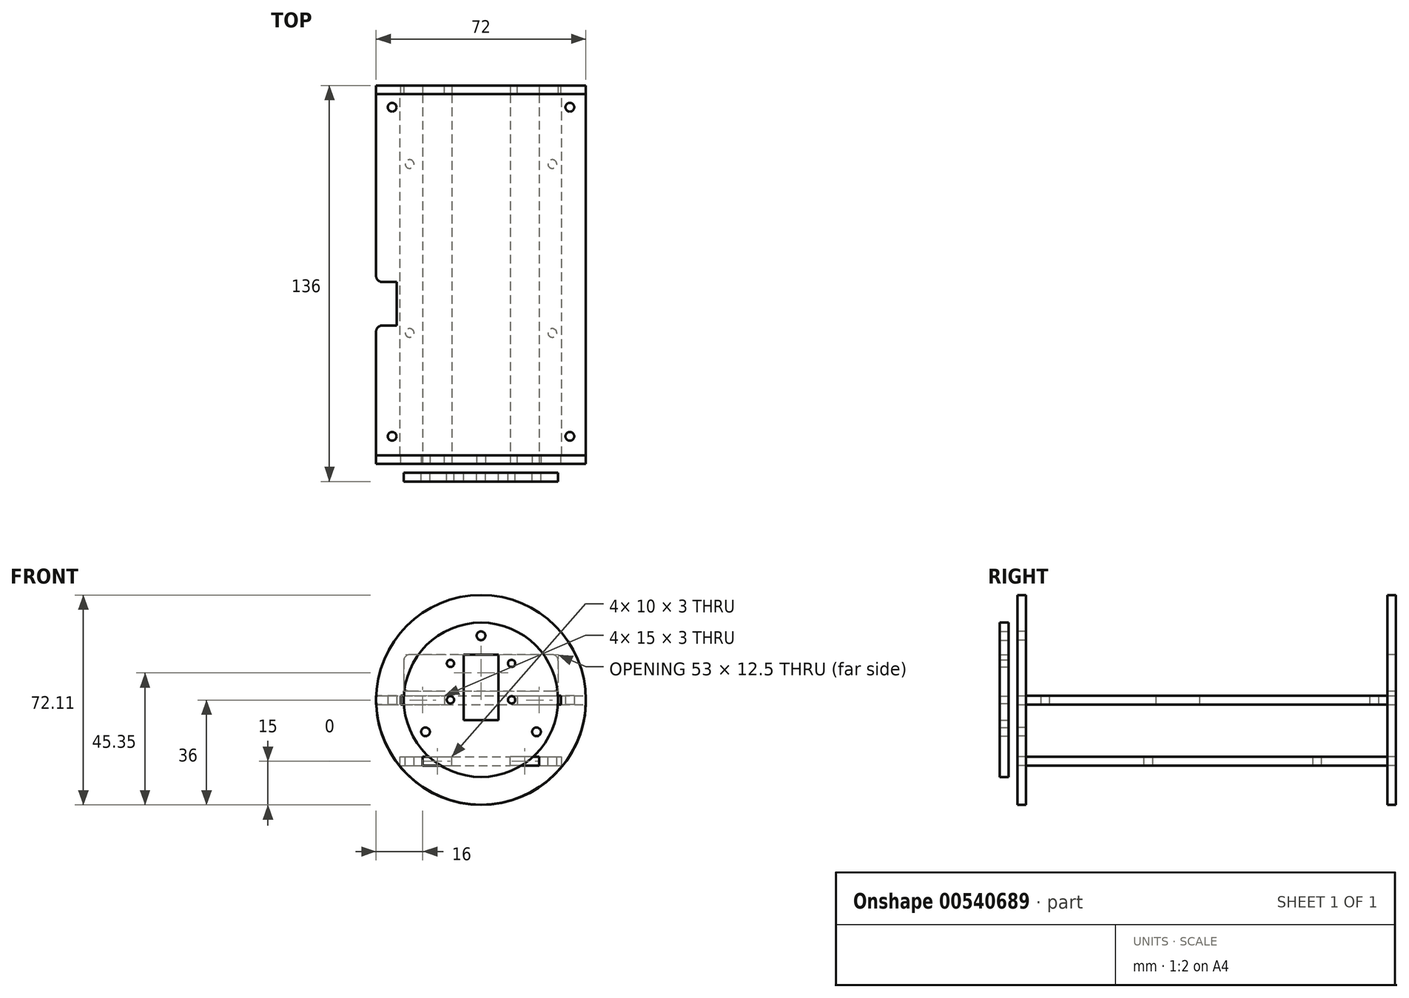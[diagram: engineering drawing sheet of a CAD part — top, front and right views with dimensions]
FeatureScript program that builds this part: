
annotation { "Feature Type Name" : "Feature", "Feature Type Description" : "" }
export const myFeature = defineFeature(function(context is Context, id is Id, definition is map)
    precondition{}
    {
        {
            var Q0;
            Q0=qCreatedBy(makeId("Top.planeOp"),FACE);
            var sketch = newSketch(context, id + "F0", { "sketchPlane" : qUnion([Q0])});
            skLineSegment(sketch, "E0.bottom", {"start": v(-34, 61) * mm, "end": v(34, 61) * mm, "construction": true});
            skLineSegment(sketch, "E0.top", {"start": v(-34, -59) * mm, "end": v(34, -59) * mm, "construction": true});
            skLineSegment(sketch, "E0.left", {"start": v(-34, 61) * mm, "end": v(-34, -59) * mm, "construction": true});
            skLineSegment(sketch, "E0.right", {"start": v(34, 61) * mm, "end": v(34, -59) * mm, "construction": true});
            skPoint(sketch, "E0.middle", {"position": v(0, 0) * mm});
            skCircle(sketch, "E1", {"center": v(-30.5, 57.5) * mm, "radius": 1.5 * mm});
            skCircle(sketch, "E2", {"center": v(30.5, 57.5) * mm, "radius": 1.5 * mm});
            skCircle(sketch, "E3", {"center": v(-30.5, -55.5) * mm, "radius": 1.5 * mm});
            skCircle(sketch, "E4", {"center": v(30.5, -55.5) * mm, "radius": 1.5 * mm});
            skLineSegment(sketch, "E5.bottom", {"start": v(-36, 62) * mm, "end": v(36, 62) * mm});
            skLineSegment(sketch, "E5.top", {"start": v(-36, -62) * mm, "end": v(36, -62) * mm});
            skLineSegment(sketch, "E5.left", {"start": v(-36, 62) * mm, "end": v(-36, -62) * mm});
            skLineSegment(sketch, "E5.right", {"start": v(36, 62) * mm, "end": v(36, -62) * mm});
            skLineSegment(sketch, "E6.bottom", {"start": v(-24, -3.98) * mm, "end": v(-34, -3.98) * mm, "construction": true});
            skLineSegment(sketch, "E6.top", {"start": v(-24, -15.98) * mm, "end": v(-34, -15.98) * mm, "construction": true});
            skLineSegment(sketch, "E6.left", {"start": v(-24, -3.98) * mm, "end": v(-24, -15.98) * mm, "construction": true});
            skLineSegment(sketch, "E6.right", {"start": v(-34, -3.98) * mm, "end": v(-34, -15.98) * mm, "construction": true});
            skPoint(sketch, "E6.middle", {"position": v(-29, -9.98) * mm});
            skLineSegment(sketch, "E7", {"start": v(-36, -2.48) * mm, "end": v(-29, -2.48) * mm});
            skPoint(sketch, "E7.endSnap0", {"position": v(-29, -3.98) * mm});
            skLineSegment(sketch, "E8", {"start": v(-29, -2.48) * mm, "end": v(-29, -17.48) * mm});
            skLineSegment(sketch, "E9", {"start": v(-29, -17.48) * mm, "end": v(-36, -17.48) * mm});
            skLineSegment(sketch, "E10.bottom", {"start": v(27.5, -62) * mm, "end": v(12.5, -62) * mm});
            skLineSegment(sketch, "E10.top", {"start": v(27.5, -65) * mm, "end": v(12.5, -65) * mm});
            skLineSegment(sketch, "E10.left", {"start": v(27.5, -62) * mm, "end": v(27.5, -65) * mm});
            skLineSegment(sketch, "E10.right", {"start": v(12.5, -62) * mm, "end": v(12.5, -65) * mm});
            skPoint(sketch, "E10.middle", {"position": v(20, -63.5) * mm});
            skLineSegment(sketch, "E11", {"start": v(22.63, 0) * mm, "end": v(0, 0) * mm, "construction": true});
            skLineSegment(sketch, "E12", {"start": v(0, 0) * mm, "end": v(0, -27.49) * mm, "construction": true});
            skLineSegment(sketch, "E13.MirrorCS", {"start": v(27.5, 62) * mm, "end": v(27.5, 65) * mm});
            skLineSegment(sketch, "E14.MirrorCS", {"start": v(27.5, 65) * mm, "end": v(12.5, 65) * mm});
            skLineSegment(sketch, "E15.MirrorCS", {"start": v(12.5, 62) * mm, "end": v(12.5, 65) * mm});
            skLineSegment(sketch, "E16.MirrorCS", {"start": v(-27.5, 62) * mm, "end": v(-27.5, 65) * mm});
            skLineSegment(sketch, "E17.MirrorCS", {"start": v(-27.5, 65) * mm, "end": v(-12.5, 65) * mm});
            skLineSegment(sketch, "E18.MirrorCS", {"start": v(-12.5, 62) * mm, "end": v(-12.5, 65) * mm});
            skLineSegment(sketch, "E19.MirrorCS", {"start": v(-27.5, -62) * mm, "end": v(-27.5, -65) * mm});
            skLineSegment(sketch, "E20.MirrorCS", {"start": v(-27.5, -65) * mm, "end": v(-12.5, -65) * mm});
            skLineSegment(sketch, "E21.MirrorCS", {"start": v(-12.5, -62) * mm, "end": v(-12.5, -65) * mm});
            skSolve(sketch);
        }
        {
            var Q0;
            Q0=makeQuery(id+"F0.imprint","IMPRINT",FACE,{"disambiguationData":[TD([[makeQuery(id+"F0.imprint","IMPRINT",EDGE,{"derivedFrom":sQuery(id+"F0.wireOp",EDGE,"E1")}),-1.0]])]});
            var Q1;
            {var subQ0=sQuery(id+"F0.wireOp",EDGE,"E13.MirrorCS");Q1=makeQuery(id+"F0.imprint","IMPRINT",FACE,{"disambiguationData":[TD([[makeQuery(id+"F0.imprint","IMPRINT",EDGE,{"derivedFrom":subQ0}),1.0]])]});}
            var Q2;
            {var subQ0=sQuery(id+"F0.wireOp",EDGE,"E16.MirrorCS");Q2=makeQuery(id+"F0.imprint","IMPRINT",FACE,{"disambiguationData":[TD([[makeQuery(id+"F0.imprint","IMPRINT",EDGE,{"derivedFrom":subQ0}),-1.0]])]});}
            var Q3;
            Q3=makeQuery(id+"F0.imprint","IMPRINT",FACE,{"disambiguationData":[TD([[makeQuery(id+"F0.imprint","IMPRINT",EDGE,{"derivedFrom":sQuery(id+"F0.wireOp",EDGE,"E10.bottom")}),1.0]])]});
            var Q4;
            {var subQ0=sQuery(id+"F0.wireOp",EDGE,"E19.MirrorCS");Q4=makeQuery(id+"F0.imprint","IMPRINT",FACE,{"disambiguationData":[TD([[makeQuery(id+"F0.imprint","IMPRINT",EDGE,{"derivedFrom":subQ0}),1.0]])]});}
            extrude(context, id + "F1", {"entities" : qUnion([Q0, Q1, Q2, Q3, Q4]), "depth" : 3 * mm});
        }
        {
            var Q0;
            Q0=makeQuery(id+"F1.opExtrude","SWEPT_EDGE",EDGE,{"disambiguationData":[OSD([sQuery(id+"F0.wireOp",EDGE,"E5.left"),sQuery(id+"F0.wireOp",EDGE,"E7")])]});
            var Q1;
            Q1=makeQuery(id+"F1.opExtrude","SWEPT_EDGE",EDGE,{"disambiguationData":[OSD([sQuery(id+"F0.wireOp",EDGE,"E5.left"),sQuery(id+"F0.wireOp",EDGE,"E9")])]});
            fillet(context, id + "F2", {"entities" : qUnion([Q0, Q1]), "radius" : 2 * mm, "tangentPropagation" : true, "allowEdgeOverflow" : false});
        }
        {
            var Q0;
            {var subQ0=sQuery(id+"F0.wireOp",EDGE,"E5.top");Q0=makeQuery(id+"F1.opExtrude","SWEPT_FACE",FACE,{"disambiguationData":[OSD([subQ0]),TDD([makeQuery(id+"F0.imprint","IMPRINT",EDGE,{"disambiguationData":[TD([[makeQuery(id+"F0.imprint","INTERSECT",VERTEX,{"derivedFrom":[subQ0,sQuery(id+"F0.wireOp",EDGE,"E21.MirrorCS")]}),-1.0]])],"derivedFrom":subQ0})])]});}
            var sketch = newSketch(context, id + "F3", { "sketchPlane" : qUnion([Q0])});
            skCircle(sketch, "E22", {"center": v(0, 1.61) * mm, "radius": 36 * mm});
            skLineSegment(sketch, "E23", {"start": v(0, 0) * mm, "end": v(0, 3) * mm, "construction": true});
            skLineSegment(sketch, "E24.0", {"start": v(-27.5, 3) * mm, "end": v(-12.5, 3) * mm});
            skLineSegment(sketch, "E24.1", {"start": v(-27.5, 3) * mm, "end": v(-27.5, 0) * mm});
            skLineSegment(sketch, "E24.2", {"start": v(-27.5, 0) * mm, "end": v(-12.5, 0) * mm});
            skLineSegment(sketch, "E24.3", {"start": v(-12.5, 3) * mm, "end": v(-12.5, 0) * mm});
            skLineSegment(sketch, "E24.4", {"start": v(27.5, 3) * mm, "end": v(12.5, 3) * mm});
            skLineSegment(sketch, "E24.5", {"start": v(12.5, 3) * mm, "end": v(12.5, 0) * mm});
            skLineSegment(sketch, "E24.6", {"start": v(27.5, 0) * mm, "end": v(12.5, 0) * mm});
            skLineSegment(sketch, "E24.7", {"start": v(27.5, 3) * mm, "end": v(27.5, 0) * mm});
            skSolve(sketch);
        }
        {
            var Q0;
            Q0=qSketchRegion(id+"F3",true);
            extrude(context, id + "F4", {"entities" : qUnion([Q0]), "depth" : 3 * mm});
        }
        {
            var Q0;
            {var subQ0=sQuery(id+"F0.wireOp",EDGE,"E5.bottom");Q0=makeQuery(id+"F1.opExtrude","SWEPT_FACE",FACE,{"disambiguationData":[OSD([subQ0]),TDD([makeQuery(id+"F0.imprint","IMPRINT",EDGE,{"disambiguationData":[TD([[makeQuery(id+"F0.imprint","INTERSECT",VERTEX,{"derivedFrom":[subQ0,sQuery(id+"F0.wireOp",EDGE,"E15.MirrorCS")]}),1.0]])],"derivedFrom":subQ0})])]});}
            var sketch = newSketch(context, id + "F5", { "sketchPlane" : qUnion([Q0])});
            skLineSegment(sketch, "E25", {"start": v(0, 0) * mm, "end": v(0, 3) * mm, "construction": true});
            skPoint(sketch, "E26", {"position": v(0, 1.5) * mm});
            skCircle(sketch, "E27", {"center": v(0, 1.5) * mm, "radius": 36 * mm});
            skLineSegment(sketch, "E28.0", {"start": v(-27.5, 3) * mm, "end": v(-12.5, 3) * mm});
            skLineSegment(sketch, "E28.1", {"start": v(-27.5, 3) * mm, "end": v(-27.5, 0) * mm});
            skLineSegment(sketch, "E28.2", {"start": v(-27.5, 0) * mm, "end": v(-12.5, 0) * mm});
            skLineSegment(sketch, "E28.3", {"start": v(-12.5, 3) * mm, "end": v(-12.5, 0) * mm});
            skLineSegment(sketch, "E28.4", {"start": v(27.5, 3) * mm, "end": v(12.5, 3) * mm});
            skLineSegment(sketch, "E28.5", {"start": v(12.5, 3) * mm, "end": v(12.5, 0) * mm});
            skLineSegment(sketch, "E28.6", {"start": v(27.5, 0) * mm, "end": v(12.5, 0) * mm});
            skLineSegment(sketch, "E28.7", {"start": v(27.5, 3) * mm, "end": v(27.5, 0) * mm});
            skLineSegment(sketch, "E29.bottom", {"start": v(-24.5, 17.1) * mm, "end": v(24.5, 17.1) * mm});
            skLineSegment(sketch, "E29.top", {"start": v(-24.5, 4.6) * mm, "end": v(24.5, 4.6) * mm});
            skLineSegment(sketch, "E29.left", {"start": v(-26.5, 15.1) * mm, "end": v(-26.5, 6.6) * mm});
            skLineSegment(sketch, "E29.right", {"start": v(26.5, 15.1) * mm, "end": v(26.5, 6.6) * mm});
            skPoint(sketch, "E29.middle", {"position": v(0, 10.85) * mm});
            skPoint(sketch, "E30.visualSharp", {"position": v(-26.5, 17.1) * mm});
            skArc(sketch, "E30.filletArc", {"start": v(-24.5, 17.1) * mm, "mid": v(-25.91, 16.51) * mm, "end": v(-26.5, 15.1) * mm});
            skPoint(sketch, "E31.visualSharp", {"position": v(-26.5, 4.6) * mm});
            skArc(sketch, "E31.filletArc", {"start": v(-26.5, 6.6) * mm, "mid": v(-25.91, 5.19) * mm, "end": v(-24.5, 4.6) * mm});
            skPoint(sketch, "E32.visualSharp", {"position": v(26.5, 4.6) * mm});
            skArc(sketch, "E32.filletArc", {"start": v(24.5, 4.6) * mm, "mid": v(25.91, 5.19) * mm, "end": v(26.5, 6.6) * mm});
            skPoint(sketch, "E33.visualSharp", {"position": v(26.5, 17.1) * mm});
            skArc(sketch, "E33.filletArc", {"start": v(26.5, 15.1) * mm, "mid": v(25.91, 16.51) * mm, "end": v(24.5, 17.1) * mm});
            skSolve(sketch);
        }
        {
            var Q0;
            Q0=qSketchRegion(id+"F5",true);
            extrude(context, id + "F6", {"entities" : qUnion([Q0]), "depth" : 3 * mm});
        }
        {
            var Q0;
            Q0=makeQuery(id+"F1.opExtrude","CAP_FACE",FACE,{"disambiguationData":[OSD([sQuery(id+"F0.wireOp",EDGE,"E1"),sQuery(id+"F0.wireOp",EDGE,"E2"),sQuery(id+"F0.wireOp",EDGE,"E3"),sQuery(id+"F0.wireOp",EDGE,"E4"),sQuery(id+"F0.wireOp",EDGE,"E5.bottom"),sQuery(id+"F0.wireOp",EDGE,"E5.top"),sQuery(id+"F0.wireOp",EDGE,"E5.left"),sQuery(id+"F0.wireOp",EDGE,"E5.right"),sQuery(id+"F0.wireOp",EDGE,"E7"),sQuery(id+"F0.wireOp",EDGE,"E8"),sQuery(id+"F0.wireOp",EDGE,"E9"),sQuery(id+"F0.wireOp",EDGE,"E10.top"),sQuery(id+"F0.wireOp",EDGE,"E10.left"),sQuery(id+"F0.wireOp",EDGE,"E10.right"),sQuery(id+"F0.wireOp",EDGE,"E13.MirrorCS"),sQuery(id+"F0.wireOp",EDGE,"E14.MirrorCS"),sQuery(id+"F0.wireOp",EDGE,"E15.MirrorCS"),sQuery(id+"F0.wireOp",EDGE,"E16.MirrorCS"),sQuery(id+"F0.wireOp",EDGE,"E17.MirrorCS"),sQuery(id+"F0.wireOp",EDGE,"E18.MirrorCS"),sQuery(id+"F0.wireOp",EDGE,"E19.MirrorCS"),sQuery(id+"F0.wireOp",EDGE,"E20.MirrorCS"),sQuery(id+"F0.wireOp",EDGE,"E21.MirrorCS")])],"isStart":true});
            cPlane(context, id + "F7", {"entities" : qUnion([Q0]), "cplaneType" : CPlaneType.OFFSET, "offset" : 18 * mm, "width" : 150 * mm, "height" : 150 * mm});
        }
        {
            var Q0;
            Q0=qCreatedBy(id+"F7.planeOp",FACE);
            var sketch = newSketch(context, id + "F8", { "sketchPlane" : qUnion([Q0])});
            skLineSegment(sketch, "E34.bottom", {"start": v(-27.75, 62) * mm, "end": v(27.75, 62) * mm});
            skLineSegment(sketch, "E34.top", {"start": v(-27.75, -62) * mm, "end": v(27.75, -62) * mm});
            skLineSegment(sketch, "E34.left", {"start": v(-27.75, 62) * mm, "end": v(-27.75, -62) * mm});
            skLineSegment(sketch, "E34.right", {"start": v(27.75, 62) * mm, "end": v(27.75, -62) * mm});
            skPoint(sketch, "E34.middle", {"position": v(0, 0) * mm});
            skLineSegment(sketch, "E35.bottom", {"start": v(-20, 62) * mm, "end": v(-10, 62) * mm});
            skLineSegment(sketch, "E35.top", {"start": v(-20, 65) * mm, "end": v(-10, 65) * mm});
            skLineSegment(sketch, "E35.left", {"start": v(-20, 62) * mm, "end": v(-20, 65) * mm});
            skLineSegment(sketch, "E35.right", {"start": v(-10, 62) * mm, "end": v(-10, 65) * mm});
            skPoint(sketch, "E35.middle", {"position": v(-15, 63.5) * mm});
            skLineSegment(sketch, "E36", {"start": v(0, 27.21) * mm, "end": v(0, 0) * mm, "construction": true});
            skLineSegment(sketch, "E37", {"start": v(0, 0) * mm, "end": v(20.44, 0) * mm, "construction": true});
            skLineSegment(sketch, "E38.MirrorCS", {"start": v(10, 62) * mm, "end": v(10, 65) * mm});
            skLineSegment(sketch, "E39.MirrorCS", {"start": v(20, 65) * mm, "end": v(10, 65) * mm});
            skLineSegment(sketch, "E40.MirrorCS", {"start": v(20, 62) * mm, "end": v(20, 65) * mm});
            skLineSegment(sketch, "E41.MirrorCS", {"start": v(20, -62) * mm, "end": v(20, -65) * mm});
            skLineSegment(sketch, "E42.MirrorCS", {"start": v(20, -65) * mm, "end": v(10, -65) * mm});
            skLineSegment(sketch, "E43.MirrorCS", {"start": v(10, -62) * mm, "end": v(10, -65) * mm});
            skLineSegment(sketch, "E44.MirrorCS", {"start": v(-10, -62) * mm, "end": v(-10, -65) * mm});
            skLineSegment(sketch, "E45.MirrorCS", {"start": v(-20, -65) * mm, "end": v(-10, -65) * mm});
            skLineSegment(sketch, "E46.MirrorCS", {"start": v(-20, -62) * mm, "end": v(-20, -65) * mm});
            skCircle(sketch, "E47", {"center": v(24.5, 20) * mm, "radius": 1.5 * mm});
            skCircle(sketch, "E48", {"center": v(24.5, -38) * mm, "radius": 1.5 * mm});
            skCircle(sketch, "E49", {"center": v(-24.5, -38) * mm, "radius": 1.5 * mm});
            skCircle(sketch, "E50", {"center": v(-24.5, 20) * mm, "radius": 1.5 * mm});
            skLineSegment(sketch, "E51", {"start": v(24.5, 20) * mm, "end": v(-24.5, 20) * mm, "construction": true});
            skPoint(sketch, "E52", {"position": v(0, 20) * mm});
            skSolve(sketch);
        }
        {
            var Q0;
            Q0=qSketchRegion(id+"F8",true);
            extrude(context, id + "F9", {"entities" : qUnion([Q0]), "depth" : 3 * mm});
        }
        {
            var Q0;
            Q0=makeQuery(id+"F4.opExtrude","CAP_FACE",FACE,{"disambiguationData":[OSD([sQuery(id+"F3.wireOp",EDGE,"E22"),sQuery(id+"F3.wireOp",EDGE,"E24.0"),sQuery(id+"F3.wireOp",EDGE,"E24.1"),sQuery(id+"F3.wireOp",EDGE,"E24.2"),sQuery(id+"F3.wireOp",EDGE,"E24.3"),sQuery(id+"F3.wireOp",EDGE,"E24.4"),sQuery(id+"F3.wireOp",EDGE,"E24.5"),sQuery(id+"F3.wireOp",EDGE,"E24.6"),sQuery(id+"F3.wireOp",EDGE,"E24.7")])],"isStart":false});
            var sketch = newSketch(context, id + "F10", { "sketchPlane" : qUnion([Q0])});
            skLineSegment(sketch, "E53.0", {"start": v(-20, -18) * mm, "end": v(-10, -18) * mm});
            skLineSegment(sketch, "E53.1", {"start": v(-20, -21) * mm, "end": v(-20, -18) * mm});
            skLineSegment(sketch, "E53.2", {"start": v(-20, -21) * mm, "end": v(-10, -21) * mm});
            skLineSegment(sketch, "E53.3", {"start": v(-10, -21) * mm, "end": v(-10, -18) * mm});
            skLineSegment(sketch, "E53.4", {"start": v(20, -18) * mm, "end": v(10, -18) * mm});
            skLineSegment(sketch, "E53.5", {"start": v(10, -21) * mm, "end": v(10, -18) * mm});
            skLineSegment(sketch, "E53.6", {"start": v(20, -21) * mm, "end": v(10, -21) * mm});
            skLineSegment(sketch, "E53.7", {"start": v(20, -21) * mm, "end": v(20, -18) * mm});
            skSolve(sketch);
        }
        {
            var Q0;
            Q0=qSketchRegion(id+"F10",true);
            var Q1;
            Q1=makeQuery(id+"F6.opExtrude","CAP_FACE",FACE,{"disambiguationData":[OSD([sQuery(id+"F5.wireOp",EDGE,"E27"),sQuery(id+"F5.wireOp",EDGE,"E28.0"),sQuery(id+"F5.wireOp",EDGE,"E28.1"),sQuery(id+"F5.wireOp",EDGE,"E28.2"),sQuery(id+"F5.wireOp",EDGE,"E28.3"),sQuery(id+"F5.wireOp",EDGE,"E28.4"),sQuery(id+"F5.wireOp",EDGE,"E28.5"),sQuery(id+"F5.wireOp",EDGE,"E28.6"),sQuery(id+"F5.wireOp",EDGE,"E28.7"),sQuery(id+"F5.wireOp",EDGE,"E29.bottom"),sQuery(id+"F5.wireOp",EDGE,"E29.top"),sQuery(id+"F5.wireOp",EDGE,"E29.left"),sQuery(id+"F5.wireOp",EDGE,"E29.right"),sQuery(id+"F5.wireOp",EDGE,"E30.filletArc"),sQuery(id+"F5.wireOp",EDGE,"E31.filletArc"),sQuery(id+"F5.wireOp",EDGE,"E32.filletArc"),sQuery(id+"F5.wireOp",EDGE,"E33.filletArc")])],"isStart":false});
            extrude(context, id + "F11", {"entities" : qUnion([Q0]), "operationType" : NewBodyOperationType.REMOVE, "endBound" : BoundingType.UP_TO_SURFACE, "oppositeDirection" : true, "endBoundEntityFace" : qUnion([Q1]), "depth" : 25 * mm});
        }
        {
            var Q0;
            Q0=makeQuery(id+"F4.opExtrude","CAP_FACE",FACE,{"disambiguationData":[OSD([sQuery(id+"F3.wireOp",EDGE,"E22"),sQuery(id+"F3.wireOp",EDGE,"E24.0"),sQuery(id+"F3.wireOp",EDGE,"E24.1"),sQuery(id+"F3.wireOp",EDGE,"E24.2"),sQuery(id+"F3.wireOp",EDGE,"E24.3"),sQuery(id+"F3.wireOp",EDGE,"E24.4"),sQuery(id+"F3.wireOp",EDGE,"E24.5"),sQuery(id+"F3.wireOp",EDGE,"E24.6"),sQuery(id+"F3.wireOp",EDGE,"E24.7")])],"isStart":false});
            cPlane(context, id + "F12", {"entities" : qUnion([Q0]), "cplaneType" : CPlaneType.OFFSET, "offset" : 3 * mm, "width" : 150 * mm, "height" : 150 * mm});
        }
        {
            var Q0;
            Q0=qCreatedBy(id+"F12.planeOp",FACE);
            var sketch = newSketch(context, id + "F13", { "sketchPlane" : qUnion([Q0])});
            skCircle(sketch, "E54.0", {"center": v(0, 1.61) * mm, "radius": 36 * mm, "construction": true});
            skLineSegment(sketch, "E55.bottom", {"start": v(-4, 5.61) * mm, "end": v(4, 5.61) * mm, "construction": true});
            skLineSegment(sketch, "E55.top", {"start": v(-4, -2.39) * mm, "end": v(4, -2.39) * mm, "construction": true});
            skLineSegment(sketch, "E55.left", {"start": v(-4, 5.61) * mm, "end": v(-4, -2.39) * mm, "construction": true});
            skLineSegment(sketch, "E55.right", {"start": v(4, 5.61) * mm, "end": v(4, -2.39) * mm, "construction": true});
            skCircle(sketch, "E56", {"center": v(-10.5, 1.61) * mm, "radius": 1.25 * mm});
            skCircle(sketch, "E57", {"center": v(10.5, 1.61) * mm, "radius": 1.25 * mm});
            skCircle(sketch, "E58", {"center": v(10.5, 14.11) * mm, "radius": 1.25 * mm});
            skCircle(sketch, "E59", {"center": v(-10.5, 14.11) * mm, "radius": 1.25 * mm});
            skLineSegment(sketch, "E60", {"start": v(-10.5, 1.61) * mm, "end": v(10.5, 1.61) * mm, "construction": true});
            skLineSegment(sketch, "E61.bottom", {"start": v(-6, 17.11) * mm, "end": v(6, 17.11) * mm});
            skLineSegment(sketch, "E61.top", {"start": v(-6, -5.39) * mm, "end": v(6, -5.39) * mm});
            skLineSegment(sketch, "E61.left", {"start": v(-6, 17.11) * mm, "end": v(-6, -5.39) * mm});
            skLineSegment(sketch, "E61.right", {"start": v(6, 17.11) * mm, "end": v(6, -5.39) * mm});
            skPoint(sketch, "E61.middle", {"position": v(0, 5.86) * mm});
            skCircle(sketch, "E62", {"center": v(0, 1.61) * mm, "radius": 26.5 * mm});
            skCircle(sketch, "E63", {"center": v(0, 23.61) * mm, "radius": 1.5 * mm});
            skCircle(sketch, "E64.1.0", {"center": v(-19.05, -9.39) * mm, "radius": 1.5 * mm});
            skCircle(sketch, "E64.2.0", {"center": v(19.05, -9.39) * mm, "radius": 1.5 * mm});
            skSolve(sketch);
        }
        {
            var Q0;
            Q0=qSketchRegion(id+"F13",true);
            extrude(context, id + "F14", {"entities" : qUnion([Q0]), "depth" : 3 * mm});
        }
        {
            var Q0;
            Q0=makeQuery(id+"F13.imprint","IMPRINT",FACE,{"disambiguationData":[TD([[makeQuery(id+"F13.imprint","IMPRINT",EDGE,{"derivedFrom":sQuery(id+"F13.wireOp",EDGE,"E63")}),1.0]])]});
            var Q1;
            Q1=makeQuery(id+"F13.imprint","IMPRINT",FACE,{"disambiguationData":[TD([[makeQuery(id+"F13.imprint","IMPRINT",EDGE,{"derivedFrom":sQuery(id+"F13.wireOp",EDGE,"E64.1.0")}),1.0]])]});
            var Q2;
            Q2=makeQuery(id+"F13.imprint","IMPRINT",FACE,{"disambiguationData":[TD([[makeQuery(id+"F13.imprint","IMPRINT",EDGE,{"derivedFrom":sQuery(id+"F13.wireOp",EDGE,"E64.2.0")}),1.0]])]});
            extrude(context, id + "F15", {"entities" : qUnion([Q0, Q1, Q2]), "operationType" : NewBodyOperationType.REMOVE, "oppositeDirection" : true, "depth" : 25 * mm});
        }
    });
